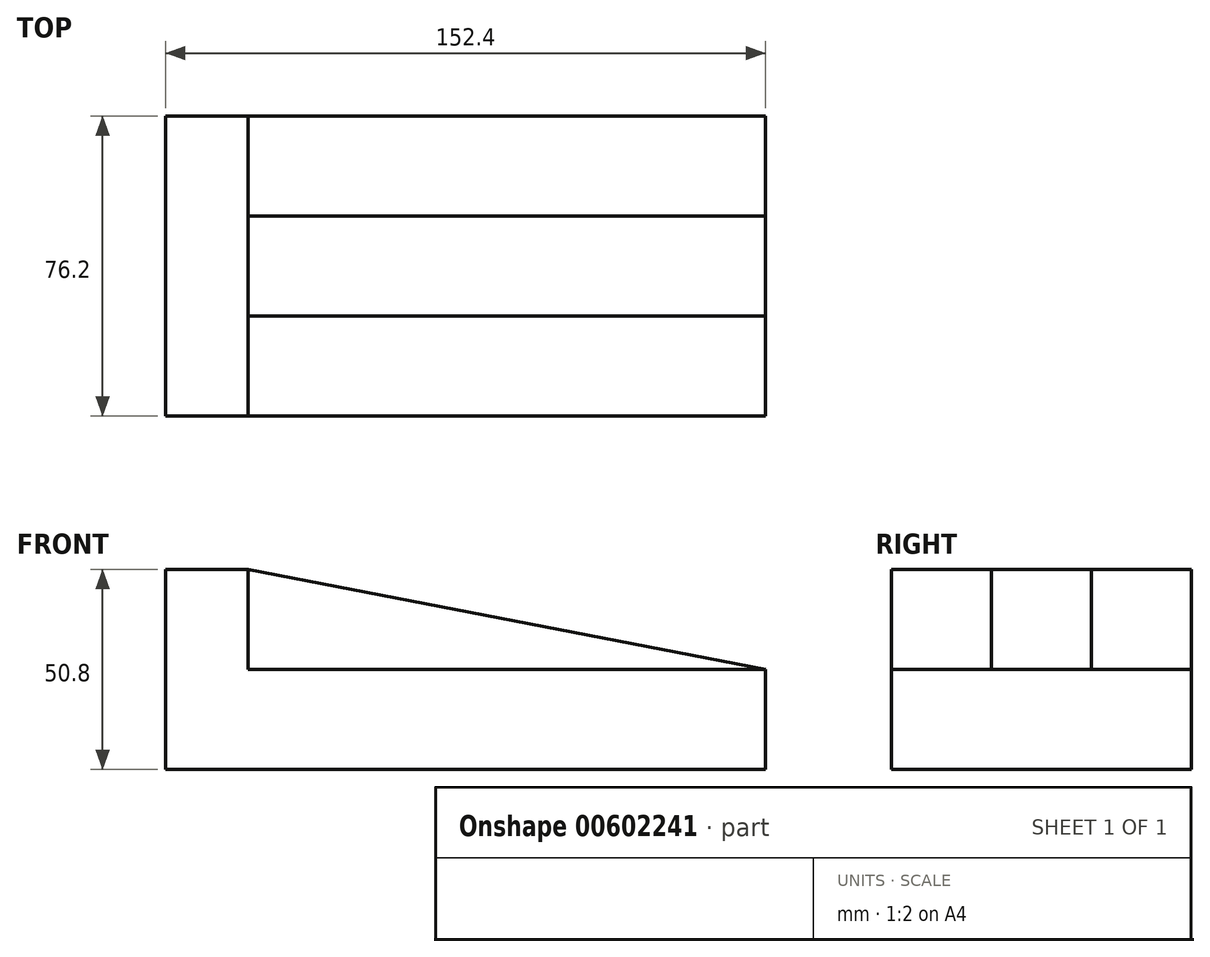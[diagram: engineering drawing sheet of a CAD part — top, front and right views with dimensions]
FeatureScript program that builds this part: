
annotation { "Feature Type Name" : "Feature", "Feature Type Description" : "" }
export const myFeature = defineFeature(function(context is Context, id is Id, definition is map)
    precondition{}
    {
        {
            var Q0;
            Q0=qCreatedBy(makeId("Front.planeOp"),FACE);
            var sketch = newSketch(context, id + "F0", { "sketchPlane" : qUnion([Q0])});
            skLineSegment(sketch, "E0", {"start": v(59.53, 0) * mm, "end": v(211.93, 0) * mm});
            skLineSegment(sketch, "E1", {"start": v(211.93, 0) * mm, "end": v(211.93, 50.8) * mm});
            skLineSegment(sketch, "E2", {"start": v(211.93, 50.8) * mm, "end": v(59.53, 50.8) * mm});
            skLineSegment(sketch, "E3", {"start": v(59.53, 50.8) * mm, "end": v(59.53, 0) * mm});
            skSolve(sketch);
        }
        {
            var Q0;
            Q0=makeQuery(id+"F0.imprint","IMPRINT",FACE,{"disambiguationData":[TD([[makeQuery(id+"F0.imprint","IMPRINT",EDGE,{"derivedFrom":sQuery(id+"F0.wireOp",EDGE,"E0")}),1.0]])]});
            extrude(context, id + "F1", {"entities" : qUnion([Q0]), "depth" : 76.2 * mm, "offsetDistance" : 25.4 * mm});
        }
        {
            var Q0;
            Q0=makeQuery(id+"F1.opExtrude","SWEPT_FACE",FACE,{"disambiguationData":[OSD([sQuery(id+"F0.wireOp",EDGE,"E2")])]});
            var sketch = newSketch(context, id + "F2", { "sketchPlane" : qUnion([Q0])});
            skLineSegment(sketch, "E4", {"start": v(80.47, -76.2) * mm, "end": v(80.47, 0) * mm});
            skLineSegment(sketch, "E5", {"start": v(80.47, -25.4) * mm, "end": v(211.93, -25.4) * mm});
            skLineSegment(sketch, "E6", {"start": v(80.47, -50.8) * mm, "end": v(211.93, -50.8) * mm});
            skLineSegment(sketch, "E7", {"start": v(80.47, -25.4) * mm, "end": v(80.47, 0) * mm});
            skLineSegment(sketch, "E8", {"start": v(80.47, -76.2) * mm, "end": v(80.47, -50.8) * mm});
            skSolve(sketch);
        }
        {
            var Q0;
            {var subQ0=sQuery(id+"F2.wireOp",EDGE,"E6");Q0=makeQuery(id+"F2.imprint","IMPRINT",FACE,{"disambiguationData":[TD([[makeQuery(id+"F2.imprint","IMPRINT",EDGE,{"derivedFrom":subQ0}),-1.0]])]});}
            extrude(context, id + "F3", {"entities" : qUnion([Q0]), "operationType" : NewBodyOperationType.REMOVE, "oppositeDirection" : true, "depth" : 25.4 * mm, "offsetDistance" : 25.4 * mm});
        }
        {
            var Q0;
            Q0=makeQuery(id+"F1.opExtrude","SWEPT_FACE",FACE,{"disambiguationData":[OSD([sQuery(id+"F0.wireOp",EDGE,"E2")])]});
            var sketch = newSketch(context, id + "F4", { "sketchPlane" : qUnion([Q0])});
            skLineSegment(sketch, "E9", {"start": v(80.47, -50.8) * mm, "end": v(80.47, 0) * mm});
            skLineSegment(sketch, "E10", {"start": v(80.47, -25.4) * mm, "end": v(211.93, -25.4) * mm});
            skLineSegment(sketch, "E11", {"start": v(80.47, -25.4) * mm, "end": v(80.47, 0) * mm});
            skSolve(sketch);
        }
        {
            var Q0;
            {var subQ0=sQuery(id+"F4.wireOp",EDGE,"E10");Q0=makeQuery(id+"F4.imprint","IMPRINT",FACE,{"disambiguationData":[TD([[makeQuery(id+"F4.imprint","IMPRINT",EDGE,{"derivedFrom":subQ0}),1.0]])]});}
            extrude(context, id + "F5", {"entities" : qUnion([Q0]), "operationType" : NewBodyOperationType.REMOVE, "oppositeDirection" : true, "depth" : 25.4 * mm, "offsetDistance" : 25.4 * mm});
        }
        {
            var Q0;
            Q0=makeQuery(id+"F3.boolean.opBoolean","COPY",FACE,{"derivedFrom":makeQuery(id+"F3.opExtrude","SWEPT_FACE",FACE,{"disambiguationData":[OSD([sQuery(id+"F2.wireOp",EDGE,"E6")])]})});
            var sketch = newSketch(context, id + "F6", { "sketchPlane" : qUnion([Q0])});
            skLineSegment(sketch, "E12", {"start": v(80.47, 50.8) * mm, "end": v(211.93, 25.4) * mm});
            skLineSegment(sketch, "E13", {"start": v(211.93, 25.4) * mm, "end": v(211.93, 50.8) * mm});
            skLineSegment(sketch, "E14", {"start": v(211.93, 50.8) * mm, "end": v(80.47, 50.8) * mm});
            skSolve(sketch);
        }
        {
            var Q0;
            Q0=makeQuery(id+"F6.imprint","IMPRINT",FACE,{"disambiguationData":[TD([[makeQuery(id+"F6.imprint","IMPRINT",EDGE,{"derivedFrom":sQuery(id+"F6.wireOp",EDGE,"E12")}),1.0]])]});
            extrude(context, id + "F7", {"entities" : qUnion([Q0]), "operationType" : NewBodyOperationType.REMOVE, "oppositeDirection" : true, "depth" : 25.4 * mm, "offsetDistance" : 25.4 * mm});
        }
    });
